# Revit family: ML 822 BI L
name_source: partatom
category: Specialty Equipment
revit_build: Autodesk Revit 2017 (Build: 20160225_1515(x64)
units: mm (PartAtom-declared; Revit-internal decimal feet)

## family parameters
Always vertical = Yes
Cut with Voids When Loaded = No
Part Type = Normal
Room Calculation Point = No
Round Connector Dimension = Use Diameter
Shared = No
Work Plane-Based = No

## types (1)
- ML 822 BIS L
    Alto = 390 mm  [stored 1.27953 ft]
    Ancho = 595 mm
    Borde Aluminio = Teka_Acero Inox
    Borde Ventilación = Teka_Acero Brillante
    Ca_1_Frecuencia Hz. = 50
    Ca_1_Potencia grill W. = 1200
    Ca_1_Potencia nominal max. W. = 2500
    Ca_1_Potencia salida mwo W. = 850
    Ca_1_Potencia turbo W. = -
    Ca_1_Tensión 220-230V = Yes
    Ca_2_Acabado Slim en acero inox antihuella = Yes
    Ca_2_Base Cerámica = Yes
    Ca_2_Botón + 1 minuto = Yes
    Ca_2_Botón + 30 segundos = No
    Ca_2_Descongelación por peso = Yes
    Ca_2_Descongelación por tiempo = Yes
    Ca_2_Funciones de cocinado = 3
    Ca_2_Grill Abatible = Yes
    Ca_2_Interior cavidad = Inox
    Ca_2_Marco de acero inox. opcional = -
    Ca_2_Menus de cocción directa = 9
    Ca_2_Microondas + Grill = Yes
    Ca_2_Niveles de potencia = 5
    Ca_2_Panel de mandos Touch Control = Yes
    Ca_2_Panel de mandos electromecánico = No
    Ca_2_Panel de mandos electrónico = No
    Ca_2_Plato giratorio integrado = No
    Ca_2_Temporizador (minutos) = 90
    Ca_2_Tipo de instalación = Integración
    Ca_3_Bloqueo de seguridad del panel = Yes
    Ca_3_Grill de cuarzo integrado = No
    Ca_3_Grill de resistencia = Yes
    Ca_3_Puerta con chip de seguridad = Yes
    Ca_3_Termostato de Seguridad = Yes
    Ca_3_Ventilación de enfriamiento = Yes
    Ca_4_Cristal Puerta = 2
    Ca_4_Parrilla para cocinado = 1
    Ca_4_Plato dorador = No
    Ca_Alto = 390 mm  [stored 1.27953 ft]
    Ca_Alto Interior = 220 mm
    Ca_Ancho = 595 mm
    Ca_Ancho Interior = 350 mm
    Ca_Capacidad en Litros = 22
    Ca_Creado por = Catálogo Arquitectura
    Ca_Código Catálogo Arquitectura = 465_TEK_015
    Ca_Código EAN = 8421152145494
    Ca_Código del Producto = 40584300
    Ca_Especificaciones Técnicas = Microondas empotrable para cocina modelo ML 822 BIS L
    Ca_Fabricante = Teka
    Ca_Instalación = Empotrado
    Ca_Itemizado CDT = E 08 06 02
    Ca_Masterformat = 11 30 13.13
    Ca_Material Principal = Acero inoxidable antihuella
    Ca_Medidas de embalaje = 450 x 645 x 440 mm
    Ca_País de Fabricación = Portugal
    Ca_Peso = 21,5 kg
    Ca_Producto = Microondas ML 822 BIS L
    Ca_Profundidad = 334 mm  [stored 1.0958 ft]
    Ca_Profundidad Interior = 280 mm
    Ca_Representante = Teka
    Ca_Teléfono = 99821 1017
    Ca_Usos = Microondas empotrable para muebles de cocina
    Ca_Web del Fabricante = www.teka.com
    Ca_Web del Representante = www.teka.cl
    Description = Microondas empotrable para muebles de cocina
    Fondo = 334 mm  [stored 1.0958 ft]
    Interior Negro = Teka_Interior Negro
    Logo Teka = Teka_Logo
    Manufacturer = Teka
    Model = ML 822 BIS L
    Panel Interior = Teka_Panel Interior
    Panel Negro = Teka_Panel Negro
    Panel Vidrio = Teka_Panel Vidrio
    Perilla Aluminio = Teka_Acero Inox
    Perilla Negro = Teka_Perilla Negro
    URL = www.teka.cl
    Voltage = 220-240

note: [stored X ft] marks values corroborated as IEEE doubles in the binary element streams (Revit-internal decimal feet)

## geometry (parser evidence)
native form markers: Sweep x2
no freeform markers — native parametric forms only
